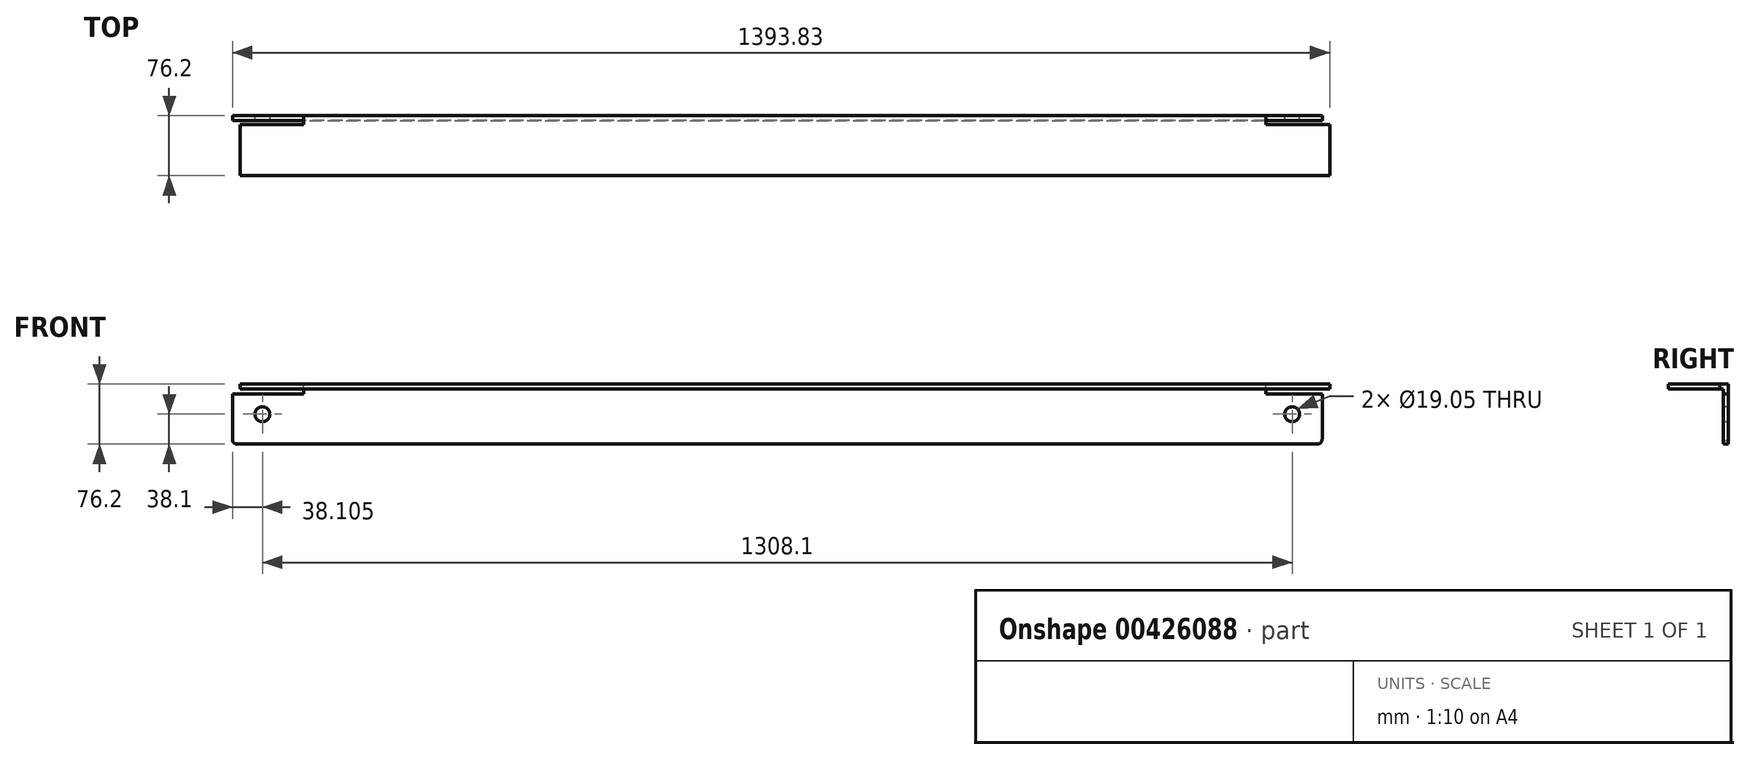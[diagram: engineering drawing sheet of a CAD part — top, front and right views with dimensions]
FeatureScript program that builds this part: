
annotation { "Feature Type Name" : "Feature", "Feature Type Description" : "" }
export const myFeature = defineFeature(function(context is Context, id is Id, definition is map)
    precondition{}
    {
        {
            var Q0;
            Q0=qCreatedBy(makeId("Front.planeOp"),FACE);
            var sketch = newSketch(context, id + "F0", { "sketchPlane" : qUnion([Q0])});
            skLineSegment(sketch, "E0.top", {"start": v(-695.51, -38.1) * mm, "end": v(676.28, -38.1) * mm});
            skPoint(sketch, "E0.middle", {"position": v(0, 0) * mm});
            skLineSegment(sketch, "E1", {"start": v(-701.67, 25.4) * mm, "end": v(-611.12, 25.4) * mm});
            skLineSegment(sketch, "E2", {"start": v(-611.12, 25.4) * mm, "end": v(-611.12, 38.1) * mm});
            skPoint(sketch, "E3.visualSharp", {"position": v(-692.15, -38.1) * mm});
            skArc(sketch, "E3.filletArc", {"start": v(-701.67, -33.27) * mm, "mid": v(-699.42, -36.75) * mm, "end": v(-695.51, -38.1) * mm});
            skLineSegment(sketch, "E4", {"start": v(-701.67, -33.27) * mm, "end": v(-701.67, 25.4) * mm});
            skLineSegment(sketch, "E5", {"start": v(611.12, 38.1) * mm, "end": v(611.12, 25.4) * mm});
            skLineSegment(sketch, "E6", {"start": v(682.63, 25.4) * mm, "end": v(611.12, 25.4) * mm});
            skPoint(sketch, "E7.visualSharp", {"position": v(692.15, -38.1) * mm});
            skArc(sketch, "E7.filletArc", {"start": v(676.28, -38.1) * mm, "mid": v(680.77, -36.24) * mm, "end": v(682.63, -31.75) * mm});
            skLineSegment(sketch, "E8", {"start": v(682.63, -31.75) * mm, "end": v(682.63, 25.4) * mm});
            skLineSegment(sketch, "E9", {"start": v(-611.12, 38.1) * mm, "end": v(611.12, 38.1) * mm});
            skCircle(sketch, "E10", {"center": v(644.53, 0) * mm, "radius": 9.53 * mm});
            skCircle(sketch, "E11", {"center": v(-663.57, 0) * mm, "radius": 9.53 * mm});
            skLineSegment(sketch, "E12", {"start": v(-611.12, 31.75) * mm, "end": v(611.12, 31.75) * mm});
            skSolve(sketch);
        }
        {
            var Q0;
            Q0=makeQuery(id+"F0.imprint","IMPRINT",FACE,{"disambiguationData":[TD([[makeQuery(id+"F0.imprint","IMPRINT",EDGE,{"derivedFrom":sQuery(id+"F0.wireOp",EDGE,"E0.top")}),1.0]])]});
            var Q1;
            {var subQ0=sQuery(id+"F0.wireOp",EDGE,"E9");Q1=makeQuery(id+"F0.imprint","IMPRINT",FACE,{"disambiguationData":[TD([[makeQuery(id+"F0.imprint","IMPRINT",EDGE,{"derivedFrom":subQ0}),-1.0]])]});}
            extrude(context, id + "F1", {"entities" : qUnion([Q0, Q1]), "depth" : 6.35 * mm});
        }
        {
            var Q0;
            Q0=makeQuery(id+"F1.opExtrude","CAP_FACE",FACE,{"disambiguationData":[OSD([sQuery(id+"F0.wireOp",EDGE,"E0.top"),sQuery(id+"F0.wireOp",EDGE,"E1"),sQuery(id+"F0.wireOp",EDGE,"E2"),sQuery(id+"F0.wireOp",EDGE,"E3.filletArc"),sQuery(id+"F0.wireOp",EDGE,"E4"),sQuery(id+"F0.wireOp",EDGE,"E5"),sQuery(id+"F0.wireOp",EDGE,"E6"),sQuery(id+"F0.wireOp",EDGE,"E7.filletArc"),sQuery(id+"F0.wireOp",EDGE,"E8"),sQuery(id+"F0.wireOp",EDGE,"E9"),sQuery(id+"F0.wireOp",EDGE,"E10"),sQuery(id+"F0.wireOp",EDGE,"E11")])],"isStart":false});
            var sketch = newSketch(context, id + "F2", { "sketchPlane" : qUnion([Q0])});
            skLineSegment(sketch, "E13", {"start": v(611.12, 31.75) * mm, "end": v(-611.12, 31.75) * mm});
            skSolve(sketch);
        }
        {
            var Q0;
            {var subQ0=sQuery(id+"F2.wireOp",EDGE,"E13");Q0=makeQuery(id+"F2.imprint","IMPRINT",FACE,{"disambiguationData":[TD([[makeQuery(id+"F2.imprint","IMPRINT",EDGE,{"derivedFrom":subQ0}),-1.0]])]});}
            extrude(context, id + "F3", {"entities" : qUnion([Q0]), "operationType" : NewBodyOperationType.ADD, "depth" : 69.85 * mm});
        }
        {
            var Q0;
            {var subQ0=sQuery(id+"F0.wireOp",EDGE,"E2");Q0=makeQuery(id+"F3.boolean.opBoolean","MERGE",FACE,{"derivedFrom":[makeQuery(id+"F1.opExtrude","SWEPT_FACE",FACE,{"disambiguationData":[OSD([subQ0])]}),makeQuery(id+"F3.opExtrude","SWEPT_FACE",FACE,{"disambiguationData":[OSD([subQ0])]})]});}
            var sketch = newSketch(context, id + "F4", { "sketchPlane" : qUnion([Q0])});
            skLineSegment(sketch, "E14", {"start": v(11.18, 31.75) * mm, "end": v(11.18, 38.1) * mm});
            skSolve(sketch);
        }
        {
            var Q0;
            Q0 = qSketchRegion(id + "F4", true);
            var Q1;
            {var subQ0=sQuery(id+"F4.wireOp",EDGE,"E14");Q1=makeQuery(id+"F4.imprint","IMPRINT",FACE,{"disambiguationData":[TD([[makeQuery(id+"F4.imprint","IMPRINT",EDGE,{"derivedFrom":subQ0}),-1.0]])]});}
            extrude(context, id + "F5", {"entities" : qUnion([Q0, Q1]), "operationType" : NewBodyOperationType.ADD, "depth" : 81.03 * mm});
        }
        {
            var Q0;
            {var subQ0=sQuery(id+"F0.wireOp",EDGE,"E5");Q0=makeQuery(id+"F3.boolean.opBoolean","MERGE",FACE,{"derivedFrom":[makeQuery(id+"F1.opExtrude","SWEPT_FACE",FACE,{"disambiguationData":[OSD([subQ0])]}),makeQuery(id+"F3.opExtrude","SWEPT_FACE",FACE,{"disambiguationData":[OSD([subQ0])]})]});}
            var sketch = newSketch(context, id + "F6", { "sketchPlane" : qUnion([Q0])});
            skLineSegment(sketch, "E15", {"start": v(-11.18, 31.75) * mm, "end": v(-11.18, 38.1) * mm});
            skSolve(sketch);
        }
        {
            var Q0;
            {var subQ0=sQuery(id+"F6.wireOp",EDGE,"E15");Q0=makeQuery(id+"F6.imprint","IMPRINT",FACE,{"disambiguationData":[TD([[makeQuery(id+"F6.imprint","IMPRINT",EDGE,{"derivedFrom":subQ0}),1.0]])]});}
            extrude(context, id + "F7", {"entities" : qUnion([Q0]), "operationType" : NewBodyOperationType.ADD, "depth" : 81.03 * mm});
        }
    });
